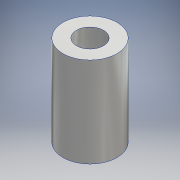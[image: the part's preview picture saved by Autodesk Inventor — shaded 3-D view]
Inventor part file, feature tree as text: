
AUTODESK INVENTOR PART (.ipt)
format: ipt  version: 2020.2 (Build 242310000, 310)  size: 104,448 bytes
history: native  units: mm
features: other x1, extrude x1, sketch x1
ambient origin geometry x8: Origin, YZ Plane, XZ Plane, XY Plane, X Axis, Y Axis, Z Axis, Center Point
bodies: Body1 (feature_tree)
feature tree (3):
  other  "ソリッド1"
  extrude  "押し出し1"  Depth=6.0mm
  sketch  "スケッチ1"
